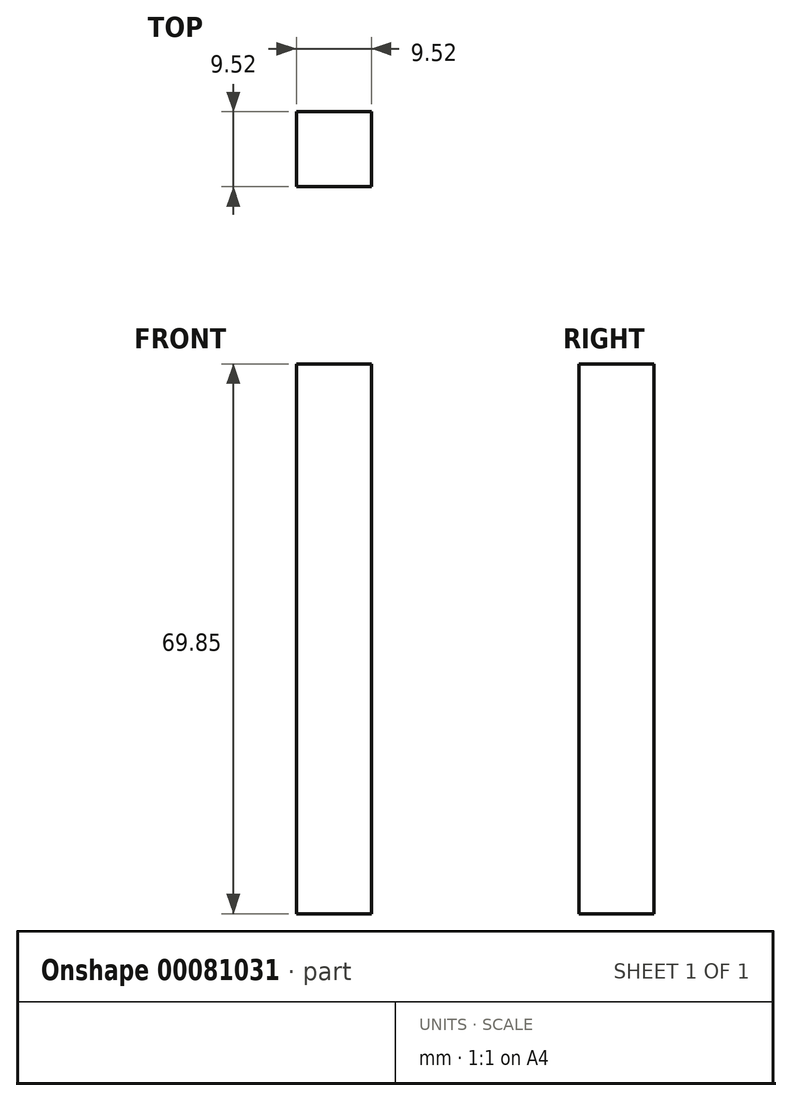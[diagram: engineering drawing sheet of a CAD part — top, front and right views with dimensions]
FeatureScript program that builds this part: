
annotation { "Feature Type Name" : "Feature", "Feature Type Description" : "" }
export const myFeature = defineFeature(function(context is Context, id is Id, definition is map)
    precondition{}
    {
        {
            var Q0;
            Q0=qCreatedBy(makeId("Top.planeOp"),FACE);
            var sketch = newSketch(context, id + "F0", { "sketchPlane" : qUnion([Q0])});
            skLineSegment(sketch, "E0.bottom", {"start": v(-4.76, 4.76) * mm, "end": v(4.76, 4.76) * mm});
            skLineSegment(sketch, "E0.top", {"start": v(-4.76, -4.76) * mm, "end": v(4.76, -4.76) * mm});
            skLineSegment(sketch, "E0.left", {"start": v(-4.76, 4.76) * mm, "end": v(-4.76, -4.76) * mm});
            skLineSegment(sketch, "E0.right", {"start": v(4.76, 4.76) * mm, "end": v(4.76, -4.76) * mm});
            skSolve(sketch);
        }
        {
            var Q0;
            Q0=makeQuery(id+"F0.imprint","IMPRINT",FACE,{"disambiguationData":[TD([[makeQuery(id+"F0.imprint","IMPRINT",EDGE,{"derivedFrom":sQuery(id+"F0.wireOp",EDGE,"E0.bottom")}),-1.0]])]});
            extrude(context, id + "F1", {"entities" : qUnion([Q0]), "depth" : 69.85 * mm});
        }
    });
